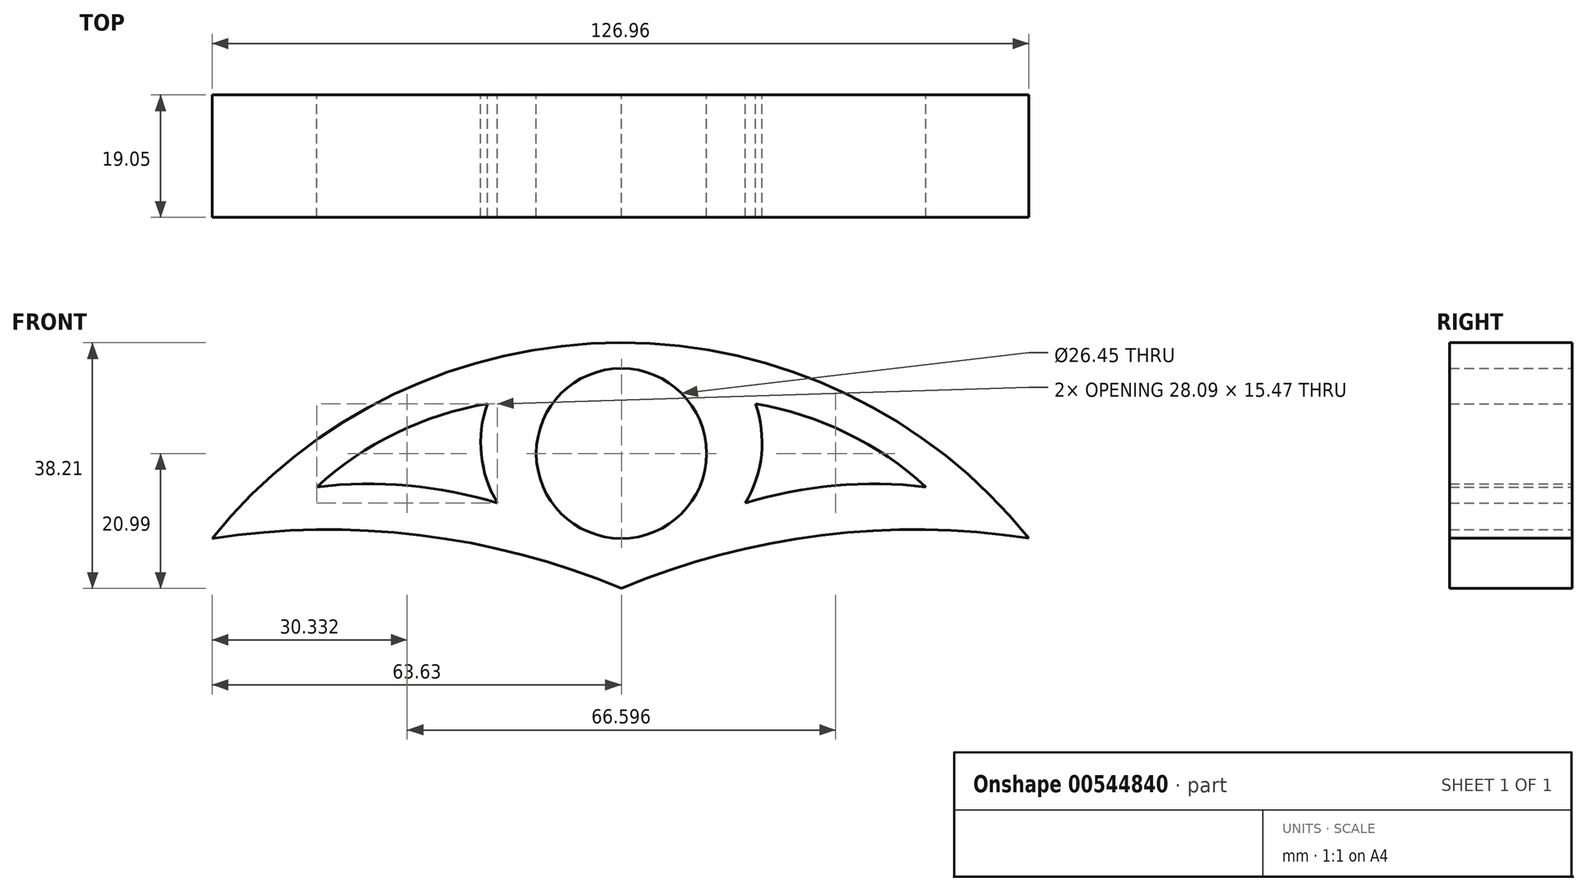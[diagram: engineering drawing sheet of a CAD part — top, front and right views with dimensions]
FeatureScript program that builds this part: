
annotation { "Feature Type Name" : "Feature", "Feature Type Description" : "" }
export const myFeature = defineFeature(function(context is Context, id is Id, definition is map)
    precondition{}
    {
        {
            var Q0;
            Q0=qCreatedBy(makeId("Front.planeOp"),FACE);
            var sketch = newSketch(context, id + "F0", { "sketchPlane" : qUnion([Q0])});
            skCircle(sketch, "E0", {"center": v(0, 0) * mm, "radius": 13.23 * mm});
            skArc(sketch, "E1", {"start": v(63.37, -13.23) * mm, "mid": v(-0.13, 17.22) * mm, "end": v(-63.63, -13.23) * mm});
            skArc(sketch, "E2", {"start": v(0, -20.99) * mm, "mid": v(-31.28, -12.71) * mm, "end": v(-63.63, -13.23) * mm});
            skArc(sketch, "E3.MirrorCS", {"start": v(0, -20.99) * mm, "mid": v(31.28, -12.71) * mm, "end": v(63.63, -13.23) * mm});
            skPoint(sketch, "E4.orphan", {"position": v(0, -13.23) * mm});
            skArc(sketch, "E5", {"start": v(-19.25, -7.73) * mm, "mid": v(-33.17, -5) * mm, "end": v(-47.34, -5.2) * mm});
            skArc(sketch, "E6", {"start": v(-20.83, 7.73) * mm, "mid": v(-35.02, 3.17) * mm, "end": v(-47.34, -5.2) * mm});
            skArc(sketch, "E7", {"start": v(-20.83, 7.73) * mm, "mid": v(-21.78, -0.18) * mm, "end": v(-19.25, -7.73) * mm});
            skArc(sketch, "E8.MirrorCS", {"start": v(20.83, 7.73) * mm, "mid": v(35.02, 3.17) * mm, "end": v(47.34, -5.2) * mm});
            skArc(sketch, "E9.MirrorCS", {"start": v(20.83, 7.73) * mm, "mid": v(21.78, -0.18) * mm, "end": v(19.25, -7.73) * mm});
            skArc(sketch, "E10.MirrorCS", {"start": v(19.25, -7.73) * mm, "mid": v(33.17, -5) * mm, "end": v(47.34, -5.2) * mm});
            skSolve(sketch);
        }
        {
            var Q0;
            Q0=makeQuery(id+"F0.imprint","IMPRINT",FACE,{"disambiguationData":[TD([[makeQuery(id+"F0.imprint","IMPRINT",EDGE,{"derivedFrom":sQuery(id+"F0.wireOp",EDGE,"E0")}),-1.0]])]});
            extrude(context, id + "F1", {"entities" : qUnion([Q0]), "depth" : 19.05 * mm, "offsetDistance" : 25.4 * mm});
        }
    });
